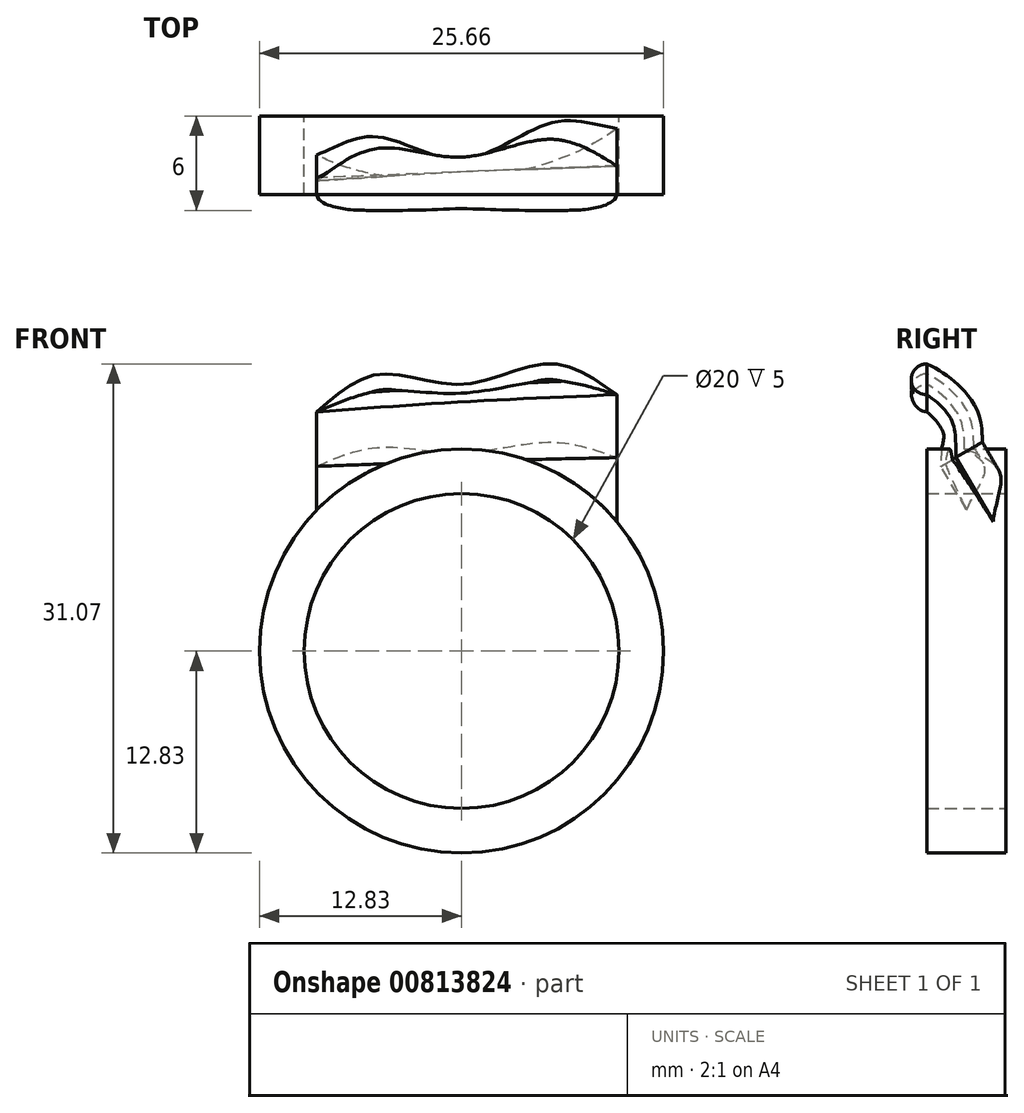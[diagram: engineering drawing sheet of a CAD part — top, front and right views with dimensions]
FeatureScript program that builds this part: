
annotation { "Feature Type Name" : "Feature", "Feature Type Description" : "" }
export const myFeature = defineFeature(function(context is Context, id is Id, definition is map)
    precondition{}
    {
        {
            var Q0;
            Q0=qCreatedBy(makeId("Front.planeOp"),FACE);
            var sketch = newSketch(context, id + "F0", { "sketchPlane" : qUnion([Q0])});
            skCircle(sketch, "E0", {"center": v(0, 0) * mm, "radius": 10 * mm});
            skCircle(sketch, "E1", {"center": v(0, 0) * mm, "radius": 12.83 * mm});
            skSolve(sketch);
        }
        {
            var Q0;
            Q0 = qSketchRegion(id + "F0", true);
            extrude(context, id + "F1", {"entities" : qUnion([Q0]), "depth" : 5 * mm, "offsetDistance" : 25 * mm});
        }
        {
            var Q0;
            Q0=makeQuery(id+"F1.opExtrude","CAP_FACE",FACE,{"disambiguationData":[OSD([sQuery(id+"F0.wireOp",EDGE,"E0"),sQuery(id+"F0.wireOp",EDGE,"E1")])],"isStart":false});
            var sketch = newSketch(context, id + "F2", { "sketchPlane" : qUnion([Q0])});
            skFitSpline(sketch, "E2", {"points": [v(-9.2, 15.2) * mm, v(-5.17, 17.59) * mm, v(0, 16.94) * mm, v(5.6, 18.24) * mm, v(9.86, 16.28) * mm], "startDerivative": vector(15.93, 14) * mm, "endDerivative": vector(16.86, -12.25) * mm});
            skFitSpline(sketch, "E3", {"points": [v(-9.2, 15.2) * mm, v(0, 15.82) * mm, v(9.86, 16.28) * mm], "startDerivative": vector(18.56, 1.37) * mm, "endDerivative": vector(19.56, 0.82) * mm});
            skSolve(sketch);
        }
        {
            var Q0;
            Q0=qCreatedBy(makeId("Right.planeOp"),FACE);
            var sketch = newSketch(context, id + "F3", { "sketchPlane" : qUnion([Q0])});
            skFitSpline(sketch, "E4", {"points": [v(-5, 16.96) * mm, v(-2.98, 15.01) * mm, v(-2.6, 12.62) * mm], "startDerivative": vector(4.2, -2.4) * mm, "endDerivative": vector(0.05, -5.14) * mm});
            skSolve(sketch);
        }
        {
            var Q0;
            Q0=makeQuery(id+"F2.imprint","IMPRINT",FACE,{"disambiguationData":[TD([[makeQuery(id+"F2.imprint","IMPRINT",EDGE,{"derivedFrom":sQuery(id+"F2.wireOp",EDGE,"E2")}),-1.0]])]});
            var Q1;
            Q1=sQuery(id+"F3.wireOp",EDGE,"E4");
            sweep(context, id + "F4", {"operationType" : NewBodyOperationType.ADD, "profiles" : qUnion([Q0]), "path" : qUnion([Q1])});
        }
        {
            var Q0;
            Q0=makeQuery(id+"F4.boolean.opBoolean","SPLIT",FACE,{"disambiguationData":[OD(0.0)],"derivedFrom":makeQuery(id+"F4.opSweep","CAP_FACE",FACE,{"disambiguationData":[OSD([sQuery(id+"F2.wireOp",EDGE,"E2"),sQuery(id+"F2.wireOp",EDGE,"E3"),sQuery(id+"F3.wireOp",VERTEX,"E4.end")])],"isStart":false})});
            var Q1;
            Q1=makeQuery(id+"F4.boolean.opBoolean","SPLIT",FACE,{"disambiguationData":[OD(1.0)],"derivedFrom":makeQuery(id+"F4.opSweep","CAP_FACE",FACE,{"disambiguationData":[OSD([sQuery(id+"F2.wireOp",EDGE,"E2"),sQuery(id+"F2.wireOp",EDGE,"E3"),sQuery(id+"F3.wireOp",VERTEX,"E4.end")])],"isStart":false})});
            extrude(context, id + "F5", {"entities" : qUnion([Q0, Q1]), "operationType" : NewBodyOperationType.ADD, "endBound" : BoundingType.UP_TO_NEXT, "depth" : 25 * mm, "offsetDistance" : 25 * mm});
        }
        {
            var Q0;
            Q0=makeQuery(id+"F4.opSweep","CAP_FACE",FACE,{"disambiguationData":[OSD([sQuery(id+"F2.wireOp",EDGE,"E2"),sQuery(id+"F2.wireOp",EDGE,"E3"),sQuery(id+"F3.wireOp",VERTEX,"E4.start")])],"isStart":true});
            extrude(context, id + "F6", {"entities" : qUnion([Q0]), "operationType" : NewBodyOperationType.ADD, "depth" : 1 * mm, "offsetDistance" : 25 * mm});
        }
        {
            var Q0;
            Q0=makeQuery(id+"F6.opExtrude","CAP_EDGE",EDGE,{"disambiguationData":[OSD([sQuery(id+"F2.wireOp",EDGE,"E3"),sQuery(id+"F3.wireOp",VERTEX,"E4.start")])],"isStart":false});
            var Q1;
            Q1=makeQuery(id+"F6.opExtrude","CAP_EDGE",EDGE,{"disambiguationData":[OSD([sQuery(id+"F2.wireOp",EDGE,"E2"),sQuery(id+"F3.wireOp",VERTEX,"E4.start")])],"isStart":false});
            fillet(context, id + "F7", {"entities" : qUnion([Q0, Q1]), "radius" : 1 * mm, "tangentPropagation" : true, "allowEdgeOverflow" : false});
        }
    });
